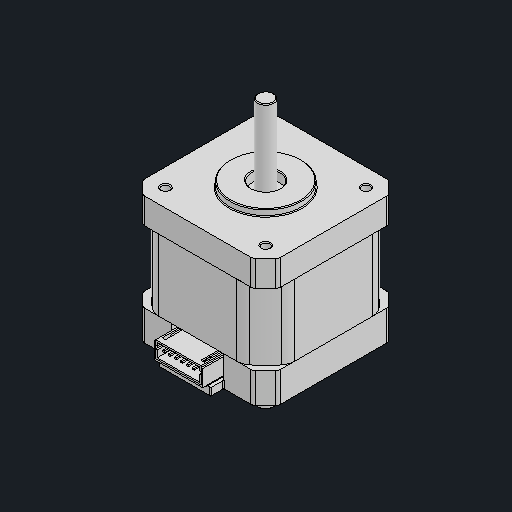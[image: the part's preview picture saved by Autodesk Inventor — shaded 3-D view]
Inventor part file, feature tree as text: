
AUTODESK INVENTOR PART (.ipt)
format: ipt  version: 2024.2 (Build 282272000, 272)  size: 419,328 bytes
history: native  units: mm
features: other x7, fillet x1, extrude x1, chamfer x1
ambient origin geometry x8: Origin, YZ Plane, XZ Plane, XY Plane, X Axis, Y Axis, Z Axis, Center Point
bodies: Body1 (feature_tree), Body2 (feature_tree), Body3 (feature_tree), Body4 (feature_tree), Body5 (feature_tree)
feature tree (10):
  other  "솔리드1"
  other  "솔리드2"
  other  "솔리드3"
  other  "솔리드4"
  other  "솔리드5"
  fillet  "Fillet6"  [1 undecoded]
  other  "M3x0.5 Tapped Hole1"
  extrude  "Extrude-Thin1"  [1 undecoded]
  other  "Boss-Extrude14"
  chamfer  "Chamfer5"  [1 undecoded]
note: 3 required parameter values undecoded (feature->parameter linkage not recoverable at this tier; creation-order binding heuristic only, values carry confidence <= 0.55)
